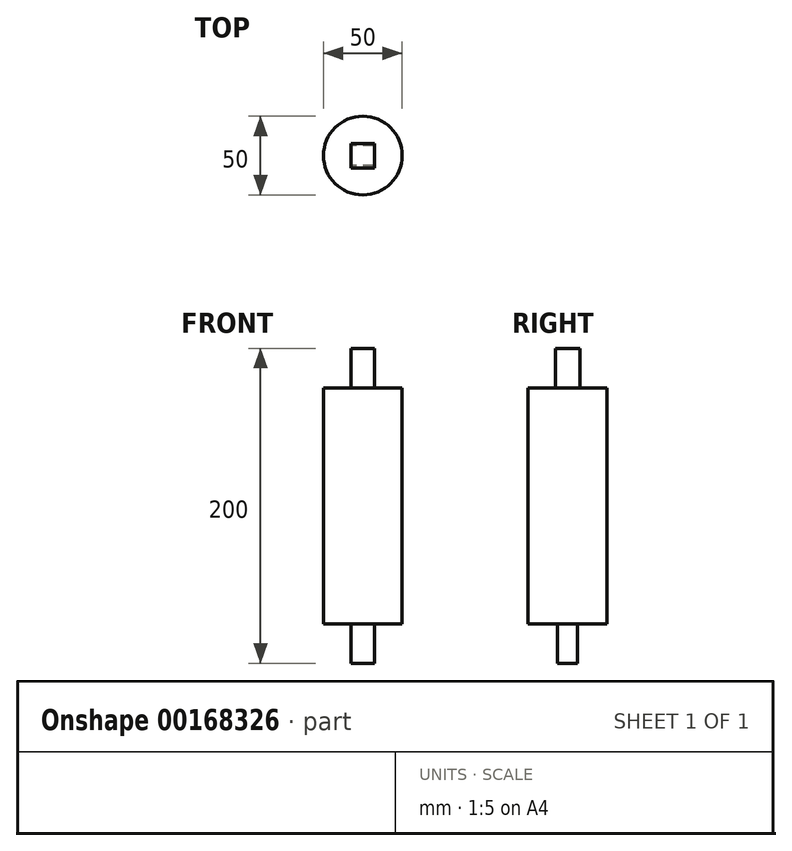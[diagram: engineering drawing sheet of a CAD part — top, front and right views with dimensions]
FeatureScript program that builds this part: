
annotation { "Feature Type Name" : "Feature", "Feature Type Description" : "" }
export const myFeature = defineFeature(function(context is Context, id is Id, definition is map)
    precondition{}
    {
        {
            var Q0;
            Q0=qCreatedBy(makeId("Top.planeOp"),FACE);
            var sketch = newSketch(context, id + "F0", { "sketchPlane" : qUnion([Q0])});
            skCircle(sketch, "E0", {"center": v(0, 0) * mm, "radius": 25 * mm});
            skSolve(sketch);
        }
        {
            var Q0;
            Q0=makeQuery(id+"F0.imprint","IMPRINT",FACE,{"disambiguationData":[TD([[makeQuery(id+"F0.imprint","IMPRINT",EDGE,{"derivedFrom":sQuery(id+"F0.wireOp",EDGE,"E0")}),1.0]])]});
            extrude(context, id + "F1", {"entities" : qUnion([Q0]), "depth" : 150 * mm});
        }
        {
            var Q0;
            Q0=makeQuery(id+"F1.opExtrude","CAP_FACE",FACE,{"disambiguationData":[OSD([sQuery(id+"F0.wireOp",EDGE,"E0")])],"isStart":false});
            var sketch = newSketch(context, id + "F2", { "sketchPlane" : qUnion([Q0])});
            skLineSegment(sketch, "E1.bottom", {"start": v(7.5, -7.77) * mm, "end": v(-7.5, -7.77) * mm});
            skLineSegment(sketch, "E1.top", {"start": v(7.5, 7.77) * mm, "end": v(-7.5, 7.77) * mm});
            skLineSegment(sketch, "E1.left", {"start": v(7.5, -7.77) * mm, "end": v(7.5, 7.77) * mm});
            skLineSegment(sketch, "E1.right", {"start": v(-7.5, -7.77) * mm, "end": v(-7.5, 7.77) * mm});
            skPoint(sketch, "E1.middle", {"position": v(0, 0) * mm});
            skSolve(sketch);
        }
        {
            var Q0;
            Q0=makeQuery(id+"F2.imprint","IMPRINT",FACE,{"disambiguationData":[TD([[makeQuery(id+"F2.imprint","IMPRINT",EDGE,{"derivedFrom":sQuery(id+"F2.wireOp",EDGE,"E1.bottom")}),-1.0]])]});
            extrude(context, id + "F3", {"entities" : qUnion([Q0]), "operationType" : NewBodyOperationType.ADD, "depth" : 25 * mm});
        }
        {
            var Q0;
            Q0=makeQuery(id+"F1.opExtrude","CAP_FACE",FACE,{"disambiguationData":[OSD([sQuery(id+"F0.wireOp",EDGE,"E0")])],"isStart":true});
            var sketch = newSketch(context, id + "F4", { "sketchPlane" : qUnion([Q0])});
            skLineSegment(sketch, "E2.bottom", {"start": v(7.5, -6.32) * mm, "end": v(-7.5, -6.32) * mm});
            skLineSegment(sketch, "E2.top", {"start": v(7.5, 6.32) * mm, "end": v(-7.5, 6.32) * mm});
            skLineSegment(sketch, "E2.left", {"start": v(7.5, -6.32) * mm, "end": v(7.5, 6.32) * mm});
            skLineSegment(sketch, "E2.right", {"start": v(-7.5, -6.32) * mm, "end": v(-7.5, 6.32) * mm});
            skPoint(sketch, "E2.middle", {"position": v(0, 0) * mm});
            skSolve(sketch);
        }
        {
            var Q0;
            Q0=makeQuery(id+"F4.imprint","IMPRINT",FACE,{"disambiguationData":[TD([[makeQuery(id+"F4.imprint","IMPRINT",EDGE,{"derivedFrom":sQuery(id+"F4.wireOp",EDGE,"E2.bottom")}),-1.0]])]});
            extrude(context, id + "F5", {"entities" : qUnion([Q0]), "operationType" : NewBodyOperationType.ADD, "depth" : 25 * mm});
        }
    });
